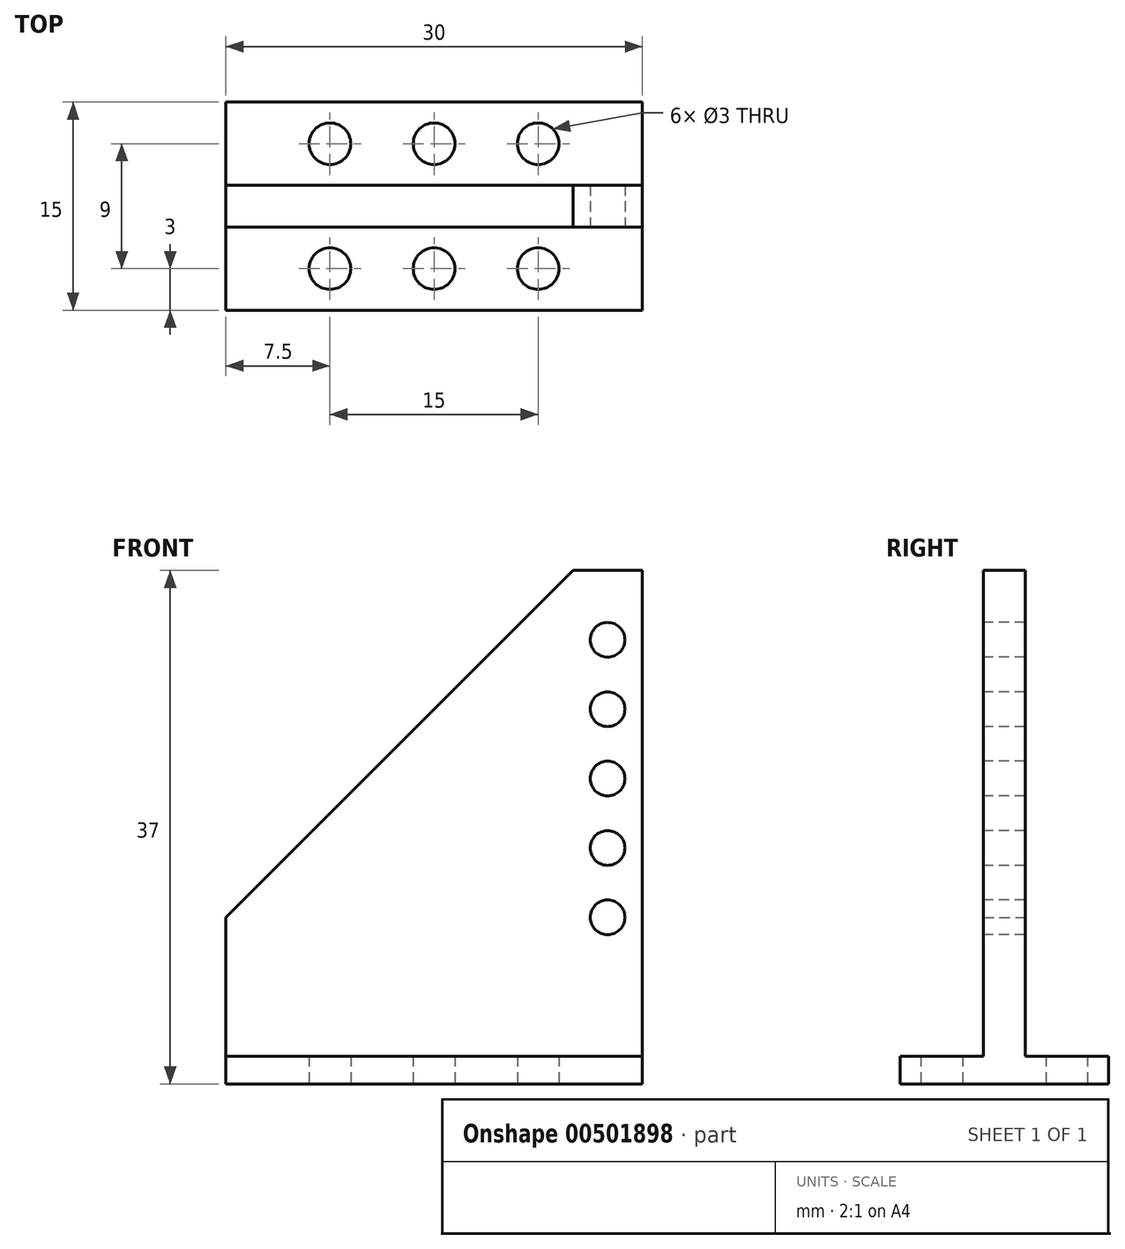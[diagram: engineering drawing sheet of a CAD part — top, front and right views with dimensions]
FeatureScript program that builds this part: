
annotation { "Feature Type Name" : "Feature", "Feature Type Description" : "" }
export const myFeature = defineFeature(function(context is Context, id is Id, definition is map)
    precondition{}
    {
        {
            var Q0;
            Q0=qCreatedBy(makeId("Top.planeOp"),FACE);
            var sketch = newSketch(context, id + "F0", { "sketchPlane" : qUnion([Q0])});
            skLineSegment(sketch, "E0.bottom", {"start": v(15, -7.5) * mm, "end": v(-15, -7.5) * mm});
            skLineSegment(sketch, "E0.top", {"start": v(15, 7.5) * mm, "end": v(-15, 7.5) * mm});
            skLineSegment(sketch, "E0.left", {"start": v(15, -7.5) * mm, "end": v(15, 7.5) * mm});
            skLineSegment(sketch, "E0.right", {"start": v(-15, -7.5) * mm, "end": v(-15, 7.5) * mm});
            skPoint(sketch, "E0.middle", {"position": v(0, 0) * mm});
            skCircle(sketch, "E1", {"center": v(0, -4.5) * mm, "radius": 1.5 * mm});
            skCircle(sketch, "E2", {"center": v(-7.5, -4.5) * mm, "radius": 1.5 * mm});
            skCircle(sketch, "E3", {"center": v(7.5, -4.5) * mm, "radius": 1.5 * mm});
            skCircle(sketch, "E4", {"center": v(-7.5, 4.5) * mm, "radius": 1.5 * mm});
            skCircle(sketch, "E5", {"center": v(0, 4.5) * mm, "radius": 1.5 * mm});
            skCircle(sketch, "E6", {"center": v(7.5, 4.5) * mm, "radius": 1.5 * mm});
            skSolve(sketch);
        }
        {
            var Q0;
            Q0 = qSketchRegion(id + "F0", true);
            var Q1;
            Q1=makeQuery(id+"F0.imprint","IMPRINT",FACE,{"disambiguationData":[TD([[makeQuery(id+"F0.imprint","IMPRINT",EDGE,{"derivedFrom":sQuery(id+"F0.wireOp",EDGE,"E0.bottom")}),-1.0]])]});
            extrude(context, id + "F1", {"entities" : qUnion([Q0, Q1]), "depth" : 2 * mm});
        }
        {
            var Q0;
            Q0=makeQuery(id+"F1.opExtrude","CAP_FACE",FACE,{"disambiguationData":[OSD([sQuery(id+"F0.wireOp",EDGE,"E0.bottom"),sQuery(id+"F0.wireOp",EDGE,"E0.top"),sQuery(id+"F0.wireOp",EDGE,"E0.left"),sQuery(id+"F0.wireOp",EDGE,"E0.right"),sQuery(id+"F0.wireOp",EDGE,"5c9VRWRa-8ECA-e6L0-femt-LMoDaafTSECn"),sQuery(id+"F0.wireOp",EDGE,"SwhFxDZ7-r8aH-dDvO-dVvK-YC1QeNDiDHFP"),sQuery(id+"F0.wireOp",EDGE,"LQyfMfmq-fHKC-VSaD-DhzT-hZpwLwdJyxLJ")])],"isStart":false});
            var sketch = newSketch(context, id + "F2", { "sketchPlane" : qUnion([Q0])});
            skLineSegment(sketch, "E7", {"start": v(15, 1.5) * mm, "end": v(-15, 1.5) * mm});
            skLineSegment(sketch, "E8", {"start": v(-15, 1.5) * mm, "end": v(-15, -1.5) * mm});
            skLineSegment(sketch, "E9", {"start": v(-15, -1.5) * mm, "end": v(15, -1.5) * mm});
            skLineSegment(sketch, "E10", {"start": v(15, 1.5) * mm, "end": v(15, -1.5) * mm});
            skSolve(sketch);
        }
        {
            var Q0;
            Q0=makeQuery(id+"F2.imprint","IMPRINT",FACE,{"disambiguationData":[TD([[makeQuery(id+"F2.imprint","IMPRINT",EDGE,{"derivedFrom":sQuery(id+"F2.wireOp",EDGE,"E7")}),1.0]])]});
            extrude(context, id + "F3", {"entities" : qUnion([Q0]), "operationType" : NewBodyOperationType.ADD, "depth" : 35 * mm});
        }
        {
            var Q0;
            Q0=makeQuery(id+"F3.opExtrude","CAP_EDGE",EDGE,{"disambiguationData":[OSD([sQuery(id+"F2.wireOp",EDGE,"E8")])],"isStart":false});
            chamfer(context, id + "F4", {"entities" : qUnion([Q0]), "width" : 25 * mm, "tangentPropagation" : true});
        }
        {
            var Q0;
            Q0=makeQuery(id+"F3.opExtrude","SWEPT_FACE",FACE,{"disambiguationData":[OSD([sQuery(id+"F2.wireOp",EDGE,"E9")])]});
            var sketch = newSketch(context, id + "F5", { "sketchPlane" : qUnion([Q0])});
            skLineSegment(sketch, "E11", {"start": v(12.5, 37) * mm, "end": v(12.5, 32) * mm});
            skLineSegment(sketch, "E12", {"start": v(12.5, 32) * mm, "end": v(12.5, 27) * mm});
            skLineSegment(sketch, "E13", {"start": v(12.5, 27) * mm, "end": v(12.5, 22) * mm});
            skLineSegment(sketch, "E14", {"start": v(12.5, 22) * mm, "end": v(12.5, 17) * mm});
            skLineSegment(sketch, "E15", {"start": v(12.5, 17) * mm, "end": v(12.5, 12) * mm});
            skSolve(sketch);
        }
        {
            var Q0;
            Q0=sQuery(id+"F5.wireOp",VERTEX,"E12.start");
            var Q1;
            Q1=sQuery(id+"F5.wireOp",VERTEX,"E13.start");
            var Q2;
            Q2=sQuery(id+"F5.wireOp",VERTEX,"E14.start");
            var Q3;
            Q3=sQuery(id+"F5.wireOp",VERTEX,"E15.start");
            var Q4;
            Q4=sQuery(id+"F5.wireOp",VERTEX,"E15.end");
            var Q5;
            Q5=makeQuery(id+"F1.opExtrude","SWEPT_BODY",BODY,{"disambiguationData":[OSD([sQuery(id+"F0.wireOp",EDGE,"E0.bottom"),sQuery(id+"F0.wireOp",EDGE,"E0.top"),sQuery(id+"F0.wireOp",EDGE,"E0.left"),sQuery(id+"F0.wireOp",EDGE,"E0.right"),sQuery(id+"F0.wireOp",EDGE,"E1"),sQuery(id+"F0.wireOp",EDGE,"E2"),sQuery(id+"F0.wireOp",EDGE,"E3"),sQuery(id+"F0.wireOp",EDGE,"E4"),sQuery(id+"F0.wireOp",EDGE,"E5"),sQuery(id+"F0.wireOp",EDGE,"E6")])]});
            hole(context, id + "F6", {"style" : HoleStyle.SIMPLE, "endStyle" : HoleEndStyle.THROUGH, "holeDiameter" : 2.5 * mm, "isTappedThrough" : true, "tappedDepth" : 12 * mm, "tapClearance" : 3, "locations" : qUnion([Q0, Q1, Q2, Q3, Q4]), "scope" : qUnion([Q5])});
        }
    });
